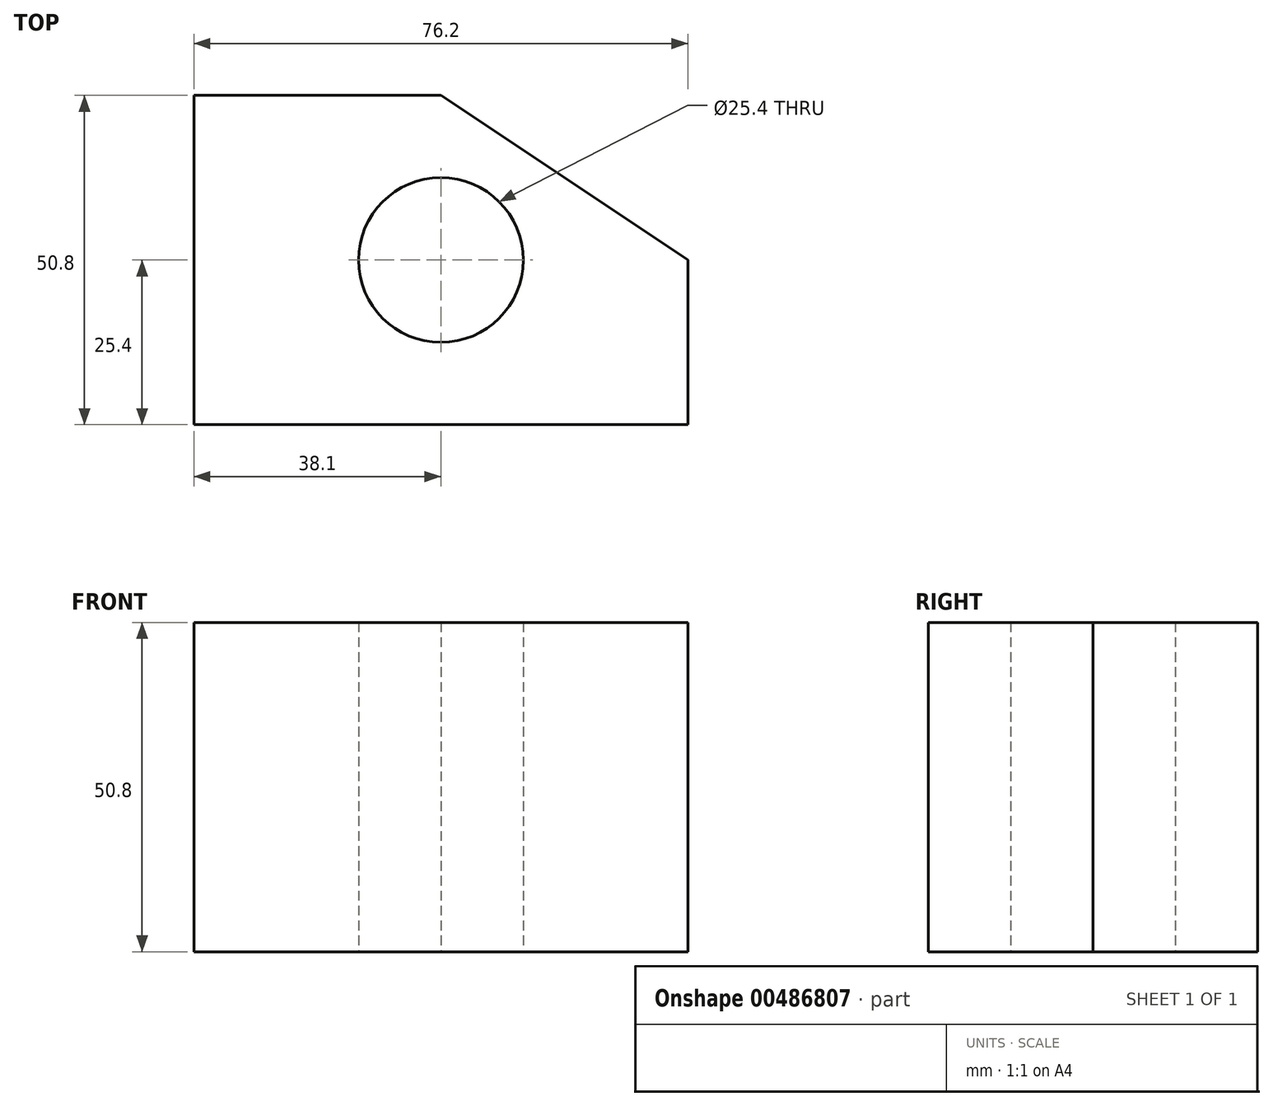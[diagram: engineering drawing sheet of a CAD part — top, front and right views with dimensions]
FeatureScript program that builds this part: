
annotation { "Feature Type Name" : "Feature", "Feature Type Description" : "" }
export const myFeature = defineFeature(function(context is Context, id is Id, definition is map)
    precondition{}
    {
        {
            var Q0;
            Q0=qCreatedBy(makeId("Top.planeOp"),FACE);
            var sketch = newSketch(context, id + "F0", { "sketchPlane" : qUnion([Q0])});
            skLineSegment(sketch, "E0.bottom", {"start": v(0, 50.8) * mm, "end": v(38.1, 50.8) * mm});
            skLineSegment(sketch, "E0.top", {"start": v(0, 0) * mm, "end": v(38.1, 0) * mm});
            skLineSegment(sketch, "E0.left", {"start": v(0, 50.8) * mm, "end": v(0, 0) * mm});
            skLineSegment(sketch, "E0.right", {"start": v(38.1, 50.8) * mm, "end": v(38.1, 0) * mm});
            skLineSegment(sketch, "E1.bottom", {"start": v(38.1, 25.4) * mm, "end": v(76.2, 25.4) * mm});
            skLineSegment(sketch, "E1.top", {"start": v(38.1, 0) * mm, "end": v(76.2, 0) * mm});
            skLineSegment(sketch, "E1.left", {"start": v(38.1, 25.4) * mm, "end": v(38.1, 0) * mm});
            skLineSegment(sketch, "E1.right", {"start": v(76.2, 25.4) * mm, "end": v(76.2, 0) * mm});
            skLineSegment(sketch, "E2", {"start": v(38.1, 50.8) * mm, "end": v(76.2, 25.4) * mm});
            skCircle(sketch, "E3", {"center": v(38.1, 25.4) * mm, "radius": 12.7 * mm});
            skSolve(sketch);
        }
        {
            var Q0;
            {var subQ1=sQuery(id+"F0.wireOp",EDGE,"E0.bottom");Q0=makeQuery(id+"F0.imprint","IMPRINT",FACE,{"disambiguationData":[TD([[makeQuery(id+"F0.imprint","IMPRINT",EDGE,{"derivedFrom":subQ1}),-1.0]])]});}
            var Q1;
            {var subQ0=sQuery(id+"F0.wireOp",EDGE,"E2");Q1=makeQuery(id+"F0.imprint","IMPRINT",FACE,{"disambiguationData":[TD([[makeQuery(id+"F0.imprint","IMPRINT",EDGE,{"derivedFrom":subQ0}),-1.0]])]});}
            var Q2;
            {var subQ2=sQuery(id+"F0.wireOp",EDGE,"E1.top");Q2=makeQuery(id+"F0.imprint","IMPRINT",FACE,{"disambiguationData":[TD([[makeQuery(id+"F0.imprint","IMPRINT",EDGE,{"derivedFrom":subQ2}),1.0]])]});}
            extrude(context, id + "F1", {"entities" : qUnion([Q0, Q1, Q2]), "depth" : 50.8 * mm});
        }
    });
